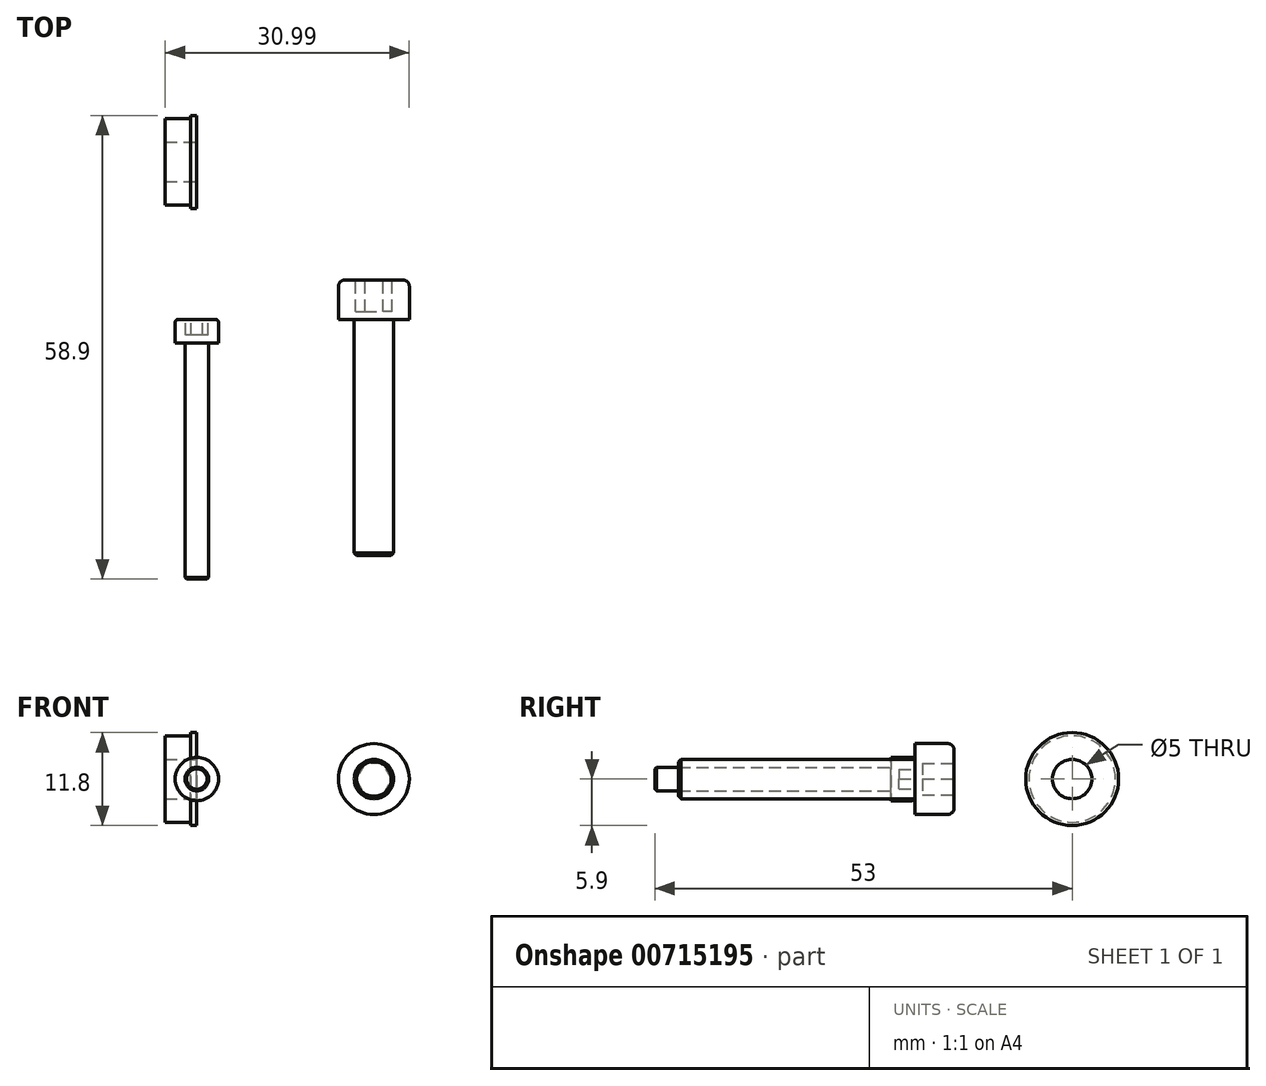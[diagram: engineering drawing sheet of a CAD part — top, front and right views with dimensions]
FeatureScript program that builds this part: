
annotation { "Feature Type Name" : "Feature", "Feature Type Description" : "" }
export const myFeature = defineFeature(function(context is Context, id is Id, definition is map)
    precondition{}
    {
        {
            var Q0;
            Q0=qCreatedBy(makeId("Front.planeOp"),FACE);
            var sketch = newSketch(context, id + "F0", { "sketchPlane" : qUnion([Q0])});
            skCircle(sketch, "E0", {"center": v(0, 0) * mm, "radius": 2.75 * mm});
            skSolve(sketch);
        }
        {
            var Q0;
            Q0=makeQuery(id+"F0.imprint","IMPRINT",FACE,{"disambiguationData":[TD([[makeQuery(id+"F0.imprint","IMPRINT",EDGE,{"derivedFrom":sQuery(id+"F0.wireOp",EDGE,"E0")}),1.0]])]});
            extrude(context, id + "F1", {"entities" : qUnion([Q0]), "depth" : 3 * mm, "offsetDistance" : 25 * mm});
        }
        {
            var Q0;
            Q0=makeQuery(id+"F1.opExtrude","CAP_FACE",FACE,{"disambiguationData":[OSD([sQuery(id+"F0.wireOp",EDGE,"E0")])],"isStart":false});
            var sketch = newSketch(context, id + "F2", { "sketchPlane" : qUnion([Q0])});
            skCircle(sketch, "E1", {"center": v(0, 0) * mm, "radius": 1.5 * mm});
            skSolve(sketch);
        }
        {
            var Q0;
            Q0=makeQuery(id+"F2.imprint","IMPRINT",FACE,{"disambiguationData":[TD([[makeQuery(id+"F2.imprint","IMPRINT",EDGE,{"derivedFrom":sQuery(id+"F2.wireOp",EDGE,"E1")}),1.0]])]});
            extrude(context, id + "F3", {"entities" : qUnion([Q0]), "operationType" : NewBodyOperationType.ADD, "depth" : 30 * mm, "offsetDistance" : 25 * mm});
        }
        {
            var Q0;
            Q0=makeQuery(id+"F3.opExtrude","CAP_EDGE",EDGE,{"disambiguationData":[OSD([sQuery(id+"F2.wireOp",EDGE,"E1")])],"isStart":false});
            chamfer(context, id + "F4", {"entities" : qUnion([Q0]), "width" : 0.2 * mm, "tangentPropagation" : true});
        }
        {
            var Q0;
            Q0=makeQuery(id+"F1.opExtrude","CAP_FACE",FACE,{"disambiguationData":[OSD([sQuery(id+"F0.wireOp",EDGE,"E0")])],"isStart":true});
            var sketch = newSketch(context, id + "F5", { "sketchPlane" : qUnion([Q0])});
            skCircle(sketch, "E2.cCircle", {"center": v(0, 0) * mm, "radius": 1.25 * mm, "construction": true});
            skLineSegment(sketch, "E2.0", {"start": v(0.72, 1.25) * mm, "end": v(1.44, 0) * mm});
            skLineSegment(sketch, "E2.1", {"start": v(1.44, 0) * mm, "end": v(0.72, -1.25) * mm});
            skLineSegment(sketch, "E2.2", {"start": v(0.72, -1.25) * mm, "end": v(-0.72, -1.25) * mm});
            skLineSegment(sketch, "E2.3", {"start": v(-0.72, -1.25) * mm, "end": v(-1.44, 0) * mm});
            skLineSegment(sketch, "E2.4", {"start": v(-1.44, 0) * mm, "end": v(-0.72, 1.25) * mm});
            skLineSegment(sketch, "E2.5", {"start": v(-0.72, 1.25) * mm, "end": v(0.72, 1.25) * mm});
            skPoint(sketch, "E2.0.midPoint", {"position": v(1.08, 0.62) * mm});
            skSolve(sketch);
        }
        {
            var Q0;
            Q0=makeQuery(id+"F5.imprint","IMPRINT",FACE,{"disambiguationData":[TD([[makeQuery(id+"F5.imprint","IMPRINT",EDGE,{"derivedFrom":sQuery(id+"F5.wireOp",EDGE,"E2.0")}),-1.0]])]});
            extrude(context, id + "F6", {"entities" : qUnion([Q0]), "operationType" : NewBodyOperationType.REMOVE, "oppositeDirection" : true, "depth" : 2 * mm, "offsetDistance" : 25 * mm});
        }
        {
            var Q0;
            Q0=makeQuery(id+"F1.opExtrude","CAP_EDGE",EDGE,{"disambiguationData":[OSD([sQuery(id+"F0.wireOp",EDGE,"E0")])],"isStart":true});
            fillet(context, id + "F7", {"entities" : qUnion([Q0]), "radius" : 0.4 * mm, "tangentPropagation" : true, "allowEdgeOverflow" : false});
        }
        {
            var Q0;
            Q0=qCreatedBy(makeId("Front.planeOp"),FACE);
            var sketch = newSketch(context, id + "F8", { "sketchPlane" : qUnion([Q0])});
            skCircle(sketch, "E3", {"center": v(22.5, 0) * mm, "radius": 2.5 * mm});
            skSolve(sketch);
        }
        {
            var Q0;
            Q0=makeQuery(id+"F8.imprint","IMPRINT",FACE,{"disambiguationData":[TD([[makeQuery(id+"F8.imprint","IMPRINT",EDGE,{"derivedFrom":sQuery(id+"F8.wireOp",EDGE,"E3")}),1.0]])]});
            extrude(context, id + "F9", {"entities" : qUnion([Q0]), "depth" : 30 * mm, "offsetDistance" : 25 * mm});
        }
        {
            var Q0;
            Q0=makeQuery(id+"F9.opExtrude","CAP_FACE",FACE,{"disambiguationData":[OSD([sQuery(id+"F8.wireOp",EDGE,"E3")])],"isStart":true});
            var sketch = newSketch(context, id + "F10", { "sketchPlane" : qUnion([Q0])});
            skCircle(sketch, "E4", {"center": v(-22.5, 0) * mm, "radius": 4.5 * mm});
            skSolve(sketch);
        }
        {
            var Q0;
            Q0=makeQuery(id+"F10.imprint","IMPRINT",FACE,{"disambiguationData":[TD([[makeQuery(id+"F10.imprint","IMPRINT",EDGE,{"derivedFrom":sQuery(id+"F10.wireOp",EDGE,"E4")}),1.0]])]});
            var Q1;
            Q1=makeQuery(id+"F10.imprint","IMPRINT",FACE,{"disambiguationData":[TD([[makeQuery(id+"F10.imprint","IMPRINT",EDGE,{"derivedFrom":makeQuery(id+"F9.opExtrude","CAP_EDGE",EDGE,{"disambiguationData":[OSD([sQuery(id+"F8.wireOp",EDGE,"E3")])],"isStart":true})}),-1.0]])]});
            extrude(context, id + "F11", {"entities" : qUnion([Q0, Q1]), "operationType" : NewBodyOperationType.ADD, "depth" : 5 * mm, "offsetDistance" : 25 * mm});
        }
        {
            var Q0;
            Q0=makeQuery(id+"F11.opExtrude","CAP_EDGE",EDGE,{"disambiguationData":[OSD([sQuery(id+"F10.wireOp",EDGE,"E4")])],"isStart":false});
            fillet(context, id + "F12", {"entities" : qUnion([Q0]), "radius" : 0.8 * mm, "tangentPropagation" : true, "allowEdgeOverflow" : false});
        }
        {
            var Q0;
            Q0=makeQuery(id+"F9.opExtrude","CAP_EDGE",EDGE,{"disambiguationData":[OSD([sQuery(id+"F8.wireOp",EDGE,"E3")])],"isStart":false});
            chamfer(context, id + "F13", {"entities" : qUnion([Q0]), "width" : 0.3 * mm, "tangentPropagation" : true});
        }
        {
            var Q0;
            Q0=makeQuery(id+"F11.opExtrude","CAP_FACE",FACE,{"disambiguationData":[OSD([sQuery(id+"F10.wireOp",EDGE,"E4")])],"isStart":false});
            var sketch = newSketch(context, id + "F14", { "sketchPlane" : qUnion([Q0])});
            skCircle(sketch, "E5.cCircle", {"center": v(-22.5, 0) * mm, "radius": 2 * mm, "construction": true});
            skLineSegment(sketch, "E5.0", {"start": v(-21.34, -2) * mm, "end": v(-23.65, -2) * mm});
            skLineSegment(sketch, "E5.1", {"start": v(-23.65, -2) * mm, "end": v(-24.8, 0) * mm});
            skLineSegment(sketch, "E5.2", {"start": v(-24.8, 0) * mm, "end": v(-23.65, 2) * mm});
            skLineSegment(sketch, "E5.3", {"start": v(-23.65, 2) * mm, "end": v(-21.34, 2) * mm});
            skLineSegment(sketch, "E5.4", {"start": v(-21.34, 2) * mm, "end": v(-20.18, 0) * mm});
            skLineSegment(sketch, "E5.5", {"start": v(-20.18, 0) * mm, "end": v(-21.34, -2) * mm});
            skPoint(sketch, "E5.0.midPoint", {"position": v(-22.5, -2) * mm});
            skSolve(sketch);
        }
        {
            var Q0;
            Q0=makeQuery(id+"F14.imprint","IMPRINT",FACE,{"disambiguationData":[TD([[makeQuery(id+"F14.imprint","IMPRINT",EDGE,{"derivedFrom":sQuery(id+"F14.wireOp",EDGE,"E5.0")}),-1.0]])]});
            extrude(context, id + "F15", {"entities" : qUnion([Q0]), "operationType" : NewBodyOperationType.REMOVE, "oppositeDirection" : true, "depth" : 4 * mm, "offsetDistance" : 25 * mm});
        }
        {
            var Q0;
            Q0=qCreatedBy(makeId("Top.planeOp"),FACE);
            var sketch = newSketch(context, id + "F16", { "sketchPlane" : qUnion([Q0])});
            skLineSegment(sketch, "E6", {"start": v(0, 20) * mm, "end": v(-12.28, 20) * mm, "construction": true});
            skLineSegment(sketch, "E7", {"start": v(0, 25.9) * mm, "end": v(-0.8, 25.9) * mm});
            skLineSegment(sketch, "E8", {"start": v(-0.8, 25.9) * mm, "end": v(-0.8, 25.5) * mm});
            skLineSegment(sketch, "E9", {"start": v(-0.8, 25.5) * mm, "end": v(-4, 25.5) * mm});
            skLineSegment(sketch, "E10", {"start": v(-4, 25.5) * mm, "end": v(-4, 22.5) * mm});
            skLineSegment(sketch, "E11", {"start": v(-4, 22.5) * mm, "end": v(0, 22.5) * mm});
            skLineSegment(sketch, "E12", {"start": v(0, 22.5) * mm, "end": v(0, 25.9) * mm});
            skSolve(sketch);
        }
        {
            var Q0;
            Q0 = qSketchRegion(id + "F16", true);
            var Q1;
            Q1=sQuery(id+"F16.wireOp",EDGE,"E6");
            revolve(context, id + "F17", {"surfaceOperationType" : NewSurfaceOperationType.NEW, "entities" : qUnion([Q0]), "axis" : qUnion([Q1]), "revolveType" : RevolveType.FULL});
        }
    });
